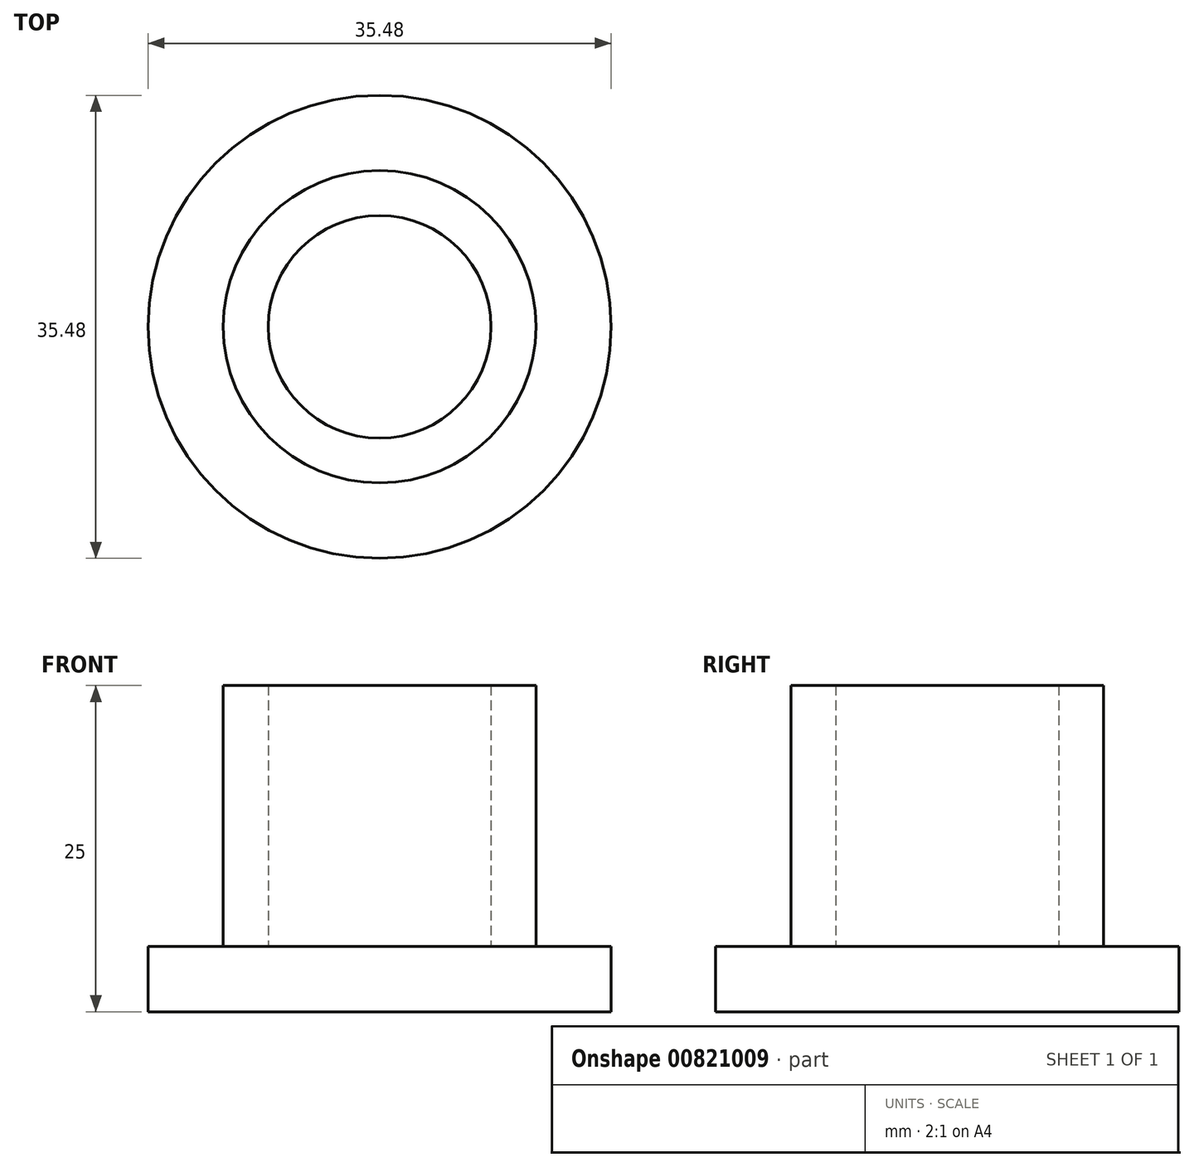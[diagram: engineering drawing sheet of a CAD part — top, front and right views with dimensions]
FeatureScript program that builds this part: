
annotation { "Feature Type Name" : "Feature", "Feature Type Description" : "" }
export const myFeature = defineFeature(function(context is Context, id is Id, definition is map)
    precondition{}
    {
        {
            var Q0;
            Q0=qCreatedBy(makeId("Top.planeOp"),FACE);
            var sketch = newSketch(context, id + "F0", { "sketchPlane" : qUnion([Q0])});
            skCircle(sketch, "E0", {"center": v(0, 0) * mm, "radius": 17.74 * mm});
            skSolve(sketch);
        }
        {
            var Q0;
            Q0=makeQuery(id+"F0.imprint","IMPRINT",FACE,{"disambiguationData":[TD([[makeQuery(id+"F0.imprint","IMPRINT",EDGE,{"derivedFrom":sQuery(id+"F0.wireOp",EDGE,"E0")}),1.0]])]});
            var sketch = newSketch(context, id + "F1", { "sketchPlane" : qUnion([Q0])});
            skCircle(sketch, "E1", {"center": v(0, 0) * mm, "radius": 11.97 * mm});
            skCircle(sketch, "E2", {"center": v(0, 0) * mm, "radius": 8.53 * mm});
            skSolve(sketch);
        }
        {
            var Q0;
            Q0=makeQuery(id+"F1.imprint","IMPRINT",FACE,{"disambiguationData":[TD([[makeQuery(id+"F1.imprint","IMPRINT",EDGE,{"derivedFrom":sQuery(id+"F1.wireOp",EDGE,"E1")}),1.0]])]});
            extrude(context, id + "F2", {"entities" : qUnion([Q0]), "depth" : 25 * mm, "offsetDistance" : 25 * mm});
        }
        {
            var Q0;
            Q0=makeQuery(id+"F0.imprint","IMPRINT",FACE,{"disambiguationData":[TD([[makeQuery(id+"F0.imprint","IMPRINT",EDGE,{"derivedFrom":sQuery(id+"F0.wireOp",EDGE,"E0")}),1.0]])]});
            extrude(context, id + "F3", {"entities" : qUnion([Q0]), "operationType" : NewBodyOperationType.ADD, "depth" : 5 * mm, "offsetDistance" : 25 * mm});
        }
    });
